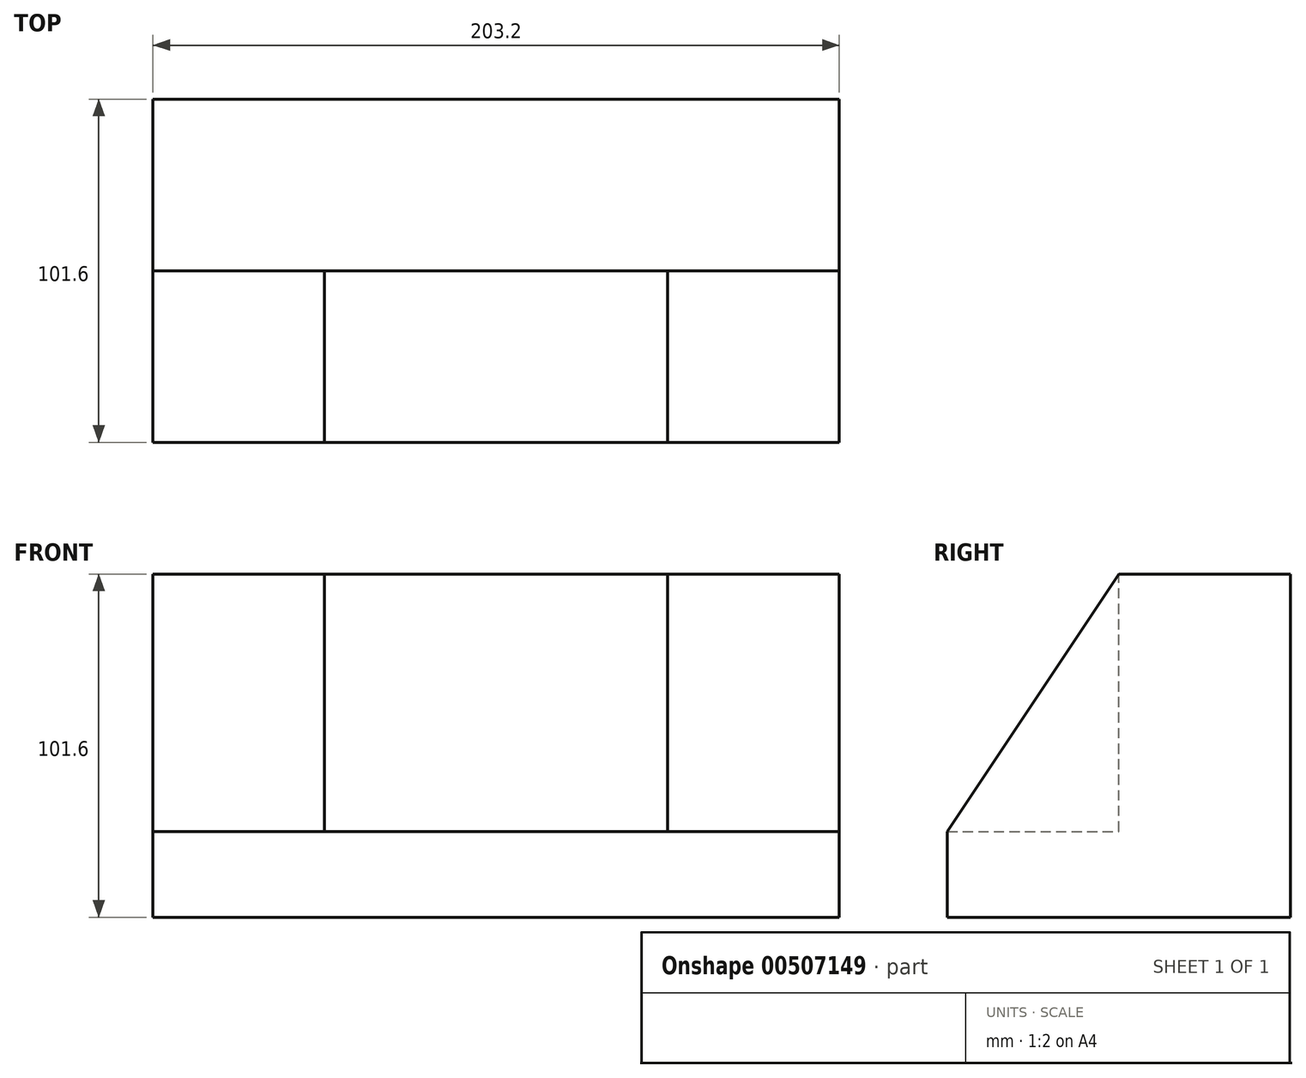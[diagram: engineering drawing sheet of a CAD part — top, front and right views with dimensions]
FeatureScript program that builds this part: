
annotation { "Feature Type Name" : "Feature", "Feature Type Description" : "" }
export const myFeature = defineFeature(function(context is Context, id is Id, definition is map)
    precondition{}
    {
        {
            var Q0;
            Q0=qCreatedBy(makeId("Front.planeOp"),FACE);
            var sketch = newSketch(context, id + "F0", { "sketchPlane" : qUnion([Q0])});
            skLineSegment(sketch, "E0.bottom", {"start": v(0, 0) * mm, "end": v(-203.2, 0) * mm});
            skLineSegment(sketch, "E0.top", {"start": v(0, 25.4) * mm, "end": v(-203.2, 25.4) * mm});
            skLineSegment(sketch, "E0.left", {"start": v(0, 0) * mm, "end": v(0, 25.4) * mm});
            skLineSegment(sketch, "E0.right", {"start": v(-203.2, 0) * mm, "end": v(-203.2, 25.4) * mm});
            skSolve(sketch);
        }
        {
            var Q0;
            Q0 = qSketchRegion(id + "F0", true);
            var Q1;
            Q1=makeQuery(id+"F0.imprint","IMPRINT",FACE,{"disambiguationData":[TD([[makeQuery(id+"F0.imprint","IMPRINT",EDGE,{"derivedFrom":sQuery(id+"F0.wireOp",EDGE,"E0.bottom")}),-1.0]])]});
            extrude(context, id + "F1", {"entities" : qUnion([Q0, Q1]), "depth" : 101.6 * mm});
        }
        {
            var Q0;
            Q0=qCreatedBy(makeId("Right.planeOp"),FACE);
            var sketch = newSketch(context, id + "F2", { "sketchPlane" : qUnion([Q0])});
            skLineSegment(sketch, "E1.bottom", {"start": v(0, 25.4) * mm, "end": v(-50.8, 25.4) * mm});
            skLineSegment(sketch, "E1.top", {"start": v(0, 101.6) * mm, "end": v(-50.8, 101.6) * mm});
            skLineSegment(sketch, "E1.left", {"start": v(0, 25.4) * mm, "end": v(0, 101.6) * mm});
            skLineSegment(sketch, "E1.right", {"start": v(-50.8, 25.4) * mm, "end": v(-50.8, 101.6) * mm});
            skSolve(sketch);
        }
        {
            var Q0;
            Q0=makeQuery(id+"F2.imprint","IMPRINT",FACE,{"disambiguationData":[TD([[makeQuery(id+"F2.imprint","IMPRINT",EDGE,{"derivedFrom":sQuery(id+"F2.wireOp",EDGE,"E1.bottom")}),-1.0]])]});
            extrude(context, id + "F3", {"entities" : qUnion([Q0]), "operationType" : NewBodyOperationType.ADD, "oppositeDirection" : true, "depth" : 203.2 * mm});
        }
        {
            var Q0;
            Q0=makeQuery(id+"F3.boolean.opBoolean","MERGE",FACE,{"derivedFrom":[makeQuery(id+"F1.opExtrude","SWEPT_FACE",FACE,{"disambiguationData":[OSD([sQuery(id+"F0.wireOp",EDGE,"E0.left")])]}),makeQuery(id+"F3.opExtrude","CAP_FACE",FACE,{"disambiguationData":[OSD([sQuery(id+"F2.wireOp",EDGE,"E1.bottom"),sQuery(id+"F2.wireOp",EDGE,"E1.top"),sQuery(id+"F2.wireOp",EDGE,"E1.left"),sQuery(id+"F2.wireOp",EDGE,"E1.right")])],"isStart":true})]});
            var sketch = newSketch(context, id + "F4", { "sketchPlane" : qUnion([Q0])});
            skLineSegment(sketch, "E2", {"start": v(-50.8, 101.6) * mm, "end": v(-101.6, 25.4) * mm});
            skLineSegment(sketch, "E3", {"start": v(-101.6, 25.4) * mm, "end": v(-50.8, 25.4) * mm});
            skLineSegment(sketch, "E4", {"start": v(-50.8, 25.4) * mm, "end": v(-50.8, 101.6) * mm});
            skSolve(sketch);
        }
        {
            var Q0;
            Q0=makeQuery(id+"F4.imprint","IMPRINT",FACE,{"disambiguationData":[TD([[makeQuery(id+"F4.imprint","IMPRINT",EDGE,{"derivedFrom":sQuery(id+"F4.wireOp",EDGE,"E2")}),1.0]])]});
            extrude(context, id + "F5", {"entities" : qUnion([Q0]), "operationType" : NewBodyOperationType.ADD, "oppositeDirection" : true, "depth" : 50.8 * mm});
        }
        {
            var Q0;
            Q0=makeQuery(id+"F3.boolean.opBoolean","MERGE",FACE,{"derivedFrom":[makeQuery(id+"F1.opExtrude","SWEPT_FACE",FACE,{"disambiguationData":[OSD([sQuery(id+"F0.wireOp",EDGE,"E0.right")])]}),makeQuery(id+"F3.opExtrude","CAP_FACE",FACE,{"disambiguationData":[OSD([sQuery(id+"F2.wireOp",EDGE,"E1.bottom"),sQuery(id+"F2.wireOp",EDGE,"E1.top"),sQuery(id+"F2.wireOp",EDGE,"E1.left"),sQuery(id+"F2.wireOp",EDGE,"E1.right")])],"isStart":false})]});
            var sketch = newSketch(context, id + "F6", { "sketchPlane" : qUnion([Q0])});
            skLineSegment(sketch, "E5", {"start": v(50.8, 101.6) * mm, "end": v(101.6, 25.4) * mm});
            skLineSegment(sketch, "E6", {"start": v(101.6, 25.4) * mm, "end": v(50.8, 25.4) * mm});
            skLineSegment(sketch, "E7", {"start": v(50.8, 25.4) * mm, "end": v(50.8, 101.6) * mm});
            skSolve(sketch);
        }
        {
            var Q0;
            Q0=makeQuery(id+"F6.imprint","IMPRINT",FACE,{"disambiguationData":[TD([[makeQuery(id+"F6.imprint","IMPRINT",EDGE,{"derivedFrom":sQuery(id+"F6.wireOp",EDGE,"E5")}),-1.0]])]});
            extrude(context, id + "F7", {"entities" : qUnion([Q0]), "operationType" : NewBodyOperationType.ADD, "oppositeDirection" : true, "depth" : 50.8 * mm});
        }
    });
